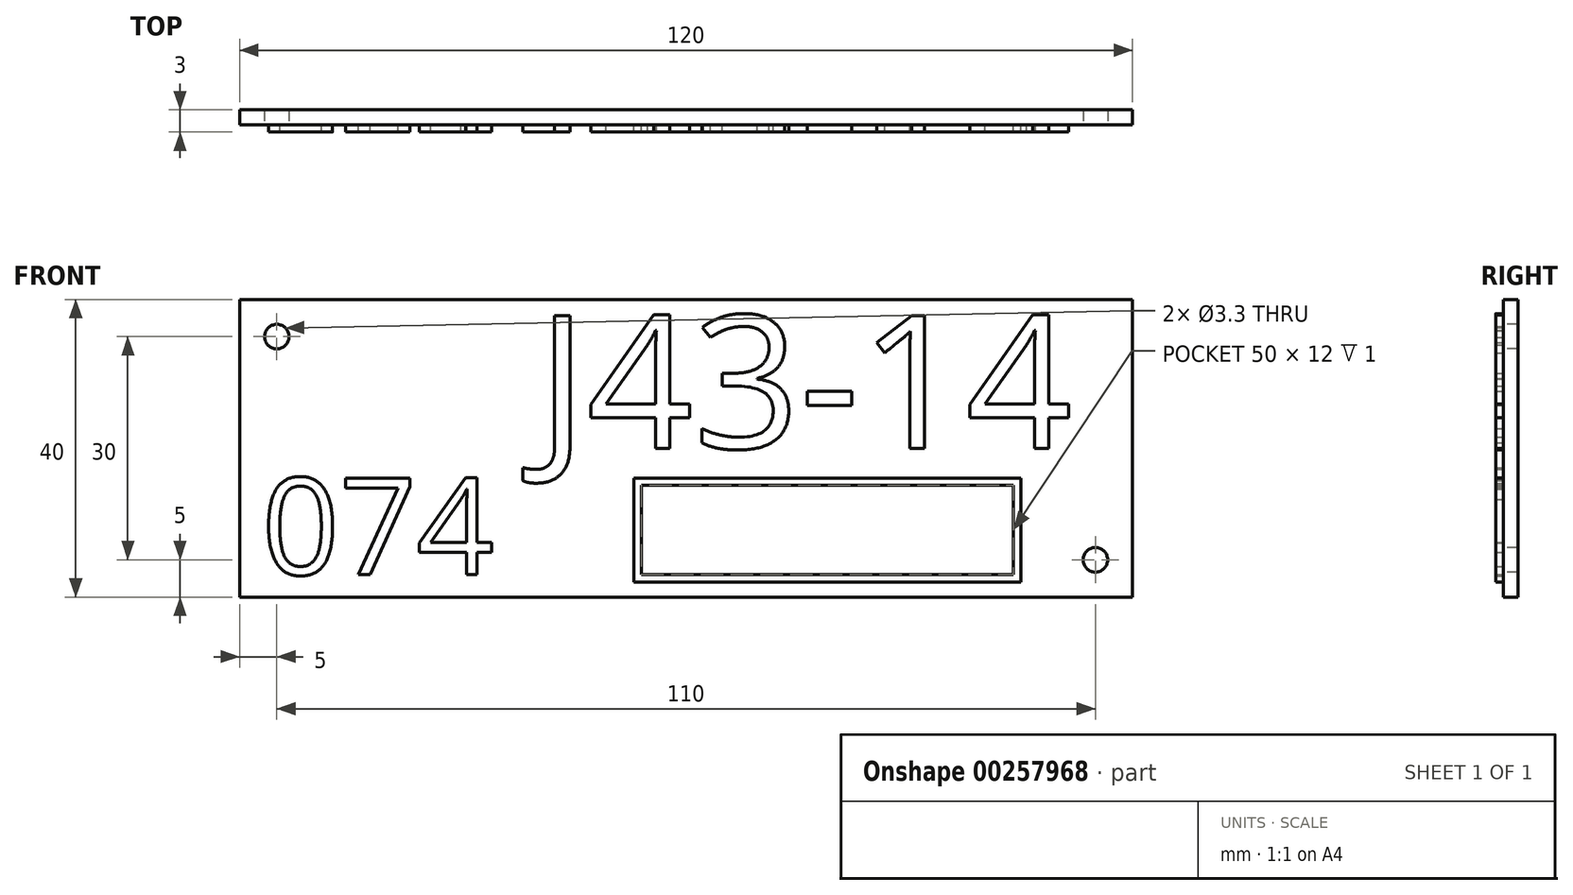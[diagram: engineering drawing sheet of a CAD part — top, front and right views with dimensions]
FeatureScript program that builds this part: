
annotation { "Feature Type Name" : "Feature", "Feature Type Description" : "" }
export const myFeature = defineFeature(function(context is Context, id is Id, definition is map)
    precondition{}
    {
        {
            var Q0;
            Q0=qCreatedBy(makeId("Front.planeOp"),FACE);
            var sketch = newSketch(context, id + "F0", { "sketchPlane" : qUnion([Q0])});
            skLineSegment(sketch, "E0.bottom", {"start": v(60, -20) * mm, "end": v(-60, -20) * mm});
            skLineSegment(sketch, "E0.top", {"start": v(60, 20) * mm, "end": v(-60, 20) * mm});
            skLineSegment(sketch, "E0.left", {"start": v(60, -20) * mm, "end": v(60, 20) * mm});
            skLineSegment(sketch, "E0.right", {"start": v(-60, -20) * mm, "end": v(-60, 20) * mm});
            skPoint(sketch, "E0.middle", {"position": v(0, 0) * mm});
            skSolve(sketch);
        }
        {
            var Q0;
            Q0=makeQuery(id+"F0.imprint","IMPRINT",FACE,{"disambiguationData":[TD([[makeQuery(id+"F0.imprint","IMPRINT",EDGE,{"derivedFrom":sQuery(id+"F0.wireOp",EDGE,"E0.bottom")}),-1.0]])]});
            extrude(context, id + "F1", {"entities" : qUnion([Q0]), "depth" : 2 * mm});
        }
        {
            var Q0;
            Q0=makeQuery(id+"F1.opExtrude","CAP_FACE",FACE,{"disambiguationData":[OSD([sQuery(id+"F0.wireOp",EDGE,"E0.bottom"),sQuery(id+"F0.wireOp",EDGE,"E0.top"),sQuery(id+"F0.wireOp",EDGE,"E0.left"),sQuery(id+"F0.wireOp",EDGE,"E0.right")])],"isStart":false});
            var sketch = newSketch(context, id + "F2", { "sketchPlane" : qUnion([Q0])});
            skPoint(sketch, "E1", {"position": v(-55, 15) * mm});
            skPoint(sketch, "E2", {"position": v(55, -15) * mm});
            skSolve(sketch);
        }
        {
            var Q0;
            Q0=sQuery(id+"F2.wireOp",VERTEX,"E1");
            var Q1;
            Q1=sQuery(id+"F2.wireOp",VERTEX,"E2");
            var Q2;
            Q2=makeQuery(id+"F1.opExtrude","SWEPT_BODY",BODY,{"disambiguationData":[OSD([sQuery(id+"F0.wireOp",EDGE,"E0.bottom"),sQuery(id+"F0.wireOp",EDGE,"E0.top"),sQuery(id+"F0.wireOp",EDGE,"E0.left"),sQuery(id+"F0.wireOp",EDGE,"E0.right")])]});
            hole(context, id + "F3", {"style" : HoleStyle.SIMPLE, "endStyle" : HoleEndStyle.THROUGH, "holeDiameter" : 3.3 * mm, "locations" : qUnion([Q0, Q1]), "scope" : qUnion([Q2]), "isTappedThrough" : true});
        }
        {
            var Q0;
            Q0=makeQuery(id+"F1.opExtrude","CAP_FACE",FACE,{"disambiguationData":[OSD([sQuery(id+"F0.wireOp",EDGE,"E0.bottom"),sQuery(id+"F0.wireOp",EDGE,"E0.top"),sQuery(id+"F0.wireOp",EDGE,"E0.left"),sQuery(id+"F0.wireOp",EDGE,"E0.right")])],"isStart":false});
            var sketch = newSketch(context, id + "F4", { "sketchPlane" : qUnion([Q0])});
            skText(sketch, "E3", { "text": "J43-14", "fontName": "OpenSans-Regular.ttf"});
            const initialGuessF4  = {"E3": [-0.02, 0, 1, 0, 0.018]};
            skSetInitialGuess(sketch, initialGuessF4);
            skSolve(sketch);
        }
        {
            var Q0;
            Q0=qSketchRegion(id+"F4",true);
            extrude(context, id + "F5", {"entities" : qUnion([Q0]), "operationType" : NewBodyOperationType.ADD, "depth" : 1 * mm});
        }
        {
            var Q0;
            {var subQ0=sQuery(id+"F0.wireOp",EDGE,"E0.top");var subQ1=sQuery(id+"F0.wireOp",EDGE,"E0.left");var subQ2=sQuery(id+"F0.wireOp",EDGE,"E0.right");var subQ3=sQuery(id+"F0.wireOp",EDGE,"E0.bottom");Q0=makeQuery(id+"F5.boolean.opBoolean","SPLIT",FACE,{"disambiguationData":[TD([makeQuery(id+"F1.opExtrude","SWEPT_FACE",FACE,{"disambiguationData":[OSD([subQ3])]})])],"derivedFrom":makeQuery(id+"F1.opExtrude","CAP_FACE",FACE,{"disambiguationData":[OSD([subQ3,subQ0,subQ1,subQ2])],"isStart":false})});}
            var sketch = newSketch(context, id + "F6", { "sketchPlane" : qUnion([Q0])});
            skText(sketch, "E4", { "text": "074\n", "fontName": "OpenSans-Regular.ttf"});
            const initialGuessF6  = {"E4": [-0.057, -0.017, 1, 0, 0.0131]};
            skSetInitialGuess(sketch, initialGuessF6);
            skSolve(sketch);
        }
        {
            var Q0;
            Q0=qSketchRegion(id+"F6",true);
            extrude(context, id + "F7", {"entities" : qUnion([Q0]), "operationType" : NewBodyOperationType.ADD, "depth" : 1 * mm});
        }
        {
            var Q0;
            {var subQ46=sQuery(id+"F0.wireOp",EDGE,"E0.top");var subQ48=sQuery(id+"F0.wireOp",EDGE,"E0.left");var subQ66=sQuery(id+"F0.wireOp",EDGE,"E0.right");var subQ76=sQuery(id+"F0.wireOp",EDGE,"E0.bottom");var subQ77=makeQuery(id+"F1.opExtrude","SWEPT_FACE",FACE,{"disambiguationData":[OSD([subQ76])]});Q0=makeQuery(id+"F7.boolean.opBoolean","SPLIT",FACE,{"disambiguationData":[TD([subQ77])],"derivedFrom":makeQuery(id+"F5.boolean.opBoolean","SPLIT",FACE,{"disambiguationData":[TD([subQ77])],"derivedFrom":makeQuery(id+"F1.opExtrude","CAP_FACE",FACE,{"disambiguationData":[OSD([subQ76,subQ46,subQ48,subQ66])],"isStart":false})})});}
            var sketch = newSketch(context, id + "F8", { "sketchPlane" : qUnion([Q0])});
            skLineSegment(sketch, "E5.bottom", {"start": v(45, -18) * mm, "end": v(-7, -18) * mm});
            skLineSegment(sketch, "E5.top", {"start": v(45, -4) * mm, "end": v(-7, -4) * mm});
            skLineSegment(sketch, "E5.left", {"start": v(45, -18) * mm, "end": v(45, -4) * mm});
            skLineSegment(sketch, "E5.right", {"start": v(-7, -18) * mm, "end": v(-7, -4) * mm});
            skPoint(sketch, "E5.middle", {"position": v(19, -11) * mm});
            skLineSegment(sketch, "E6.0", {"start": v(44, -5) * mm, "end": v(-6, -5) * mm});
            skLineSegment(sketch, "E6.1", {"start": v(44, -17) * mm, "end": v(44, -5) * mm});
            skLineSegment(sketch, "E6.2", {"start": v(44, -17) * mm, "end": v(-6, -17) * mm});
            skLineSegment(sketch, "E6.3", {"start": v(-6, -17) * mm, "end": v(-6, -5) * mm});
            skSolve(sketch);
        }
        {
            var Q0;
            Q0=makeQuery(id+"F8.imprint","IMPRINT",FACE,{"disambiguationData":[TD([[makeQuery(id+"F8.imprint","IMPRINT",EDGE,{"derivedFrom":sQuery(id+"F8.wireOp",EDGE,"E5.bottom")}),-1.0]])]});
            extrude(context, id + "F9", {"entities" : qUnion([Q0]), "operationType" : NewBodyOperationType.ADD, "depth" : 1 * mm});
        }
    });
